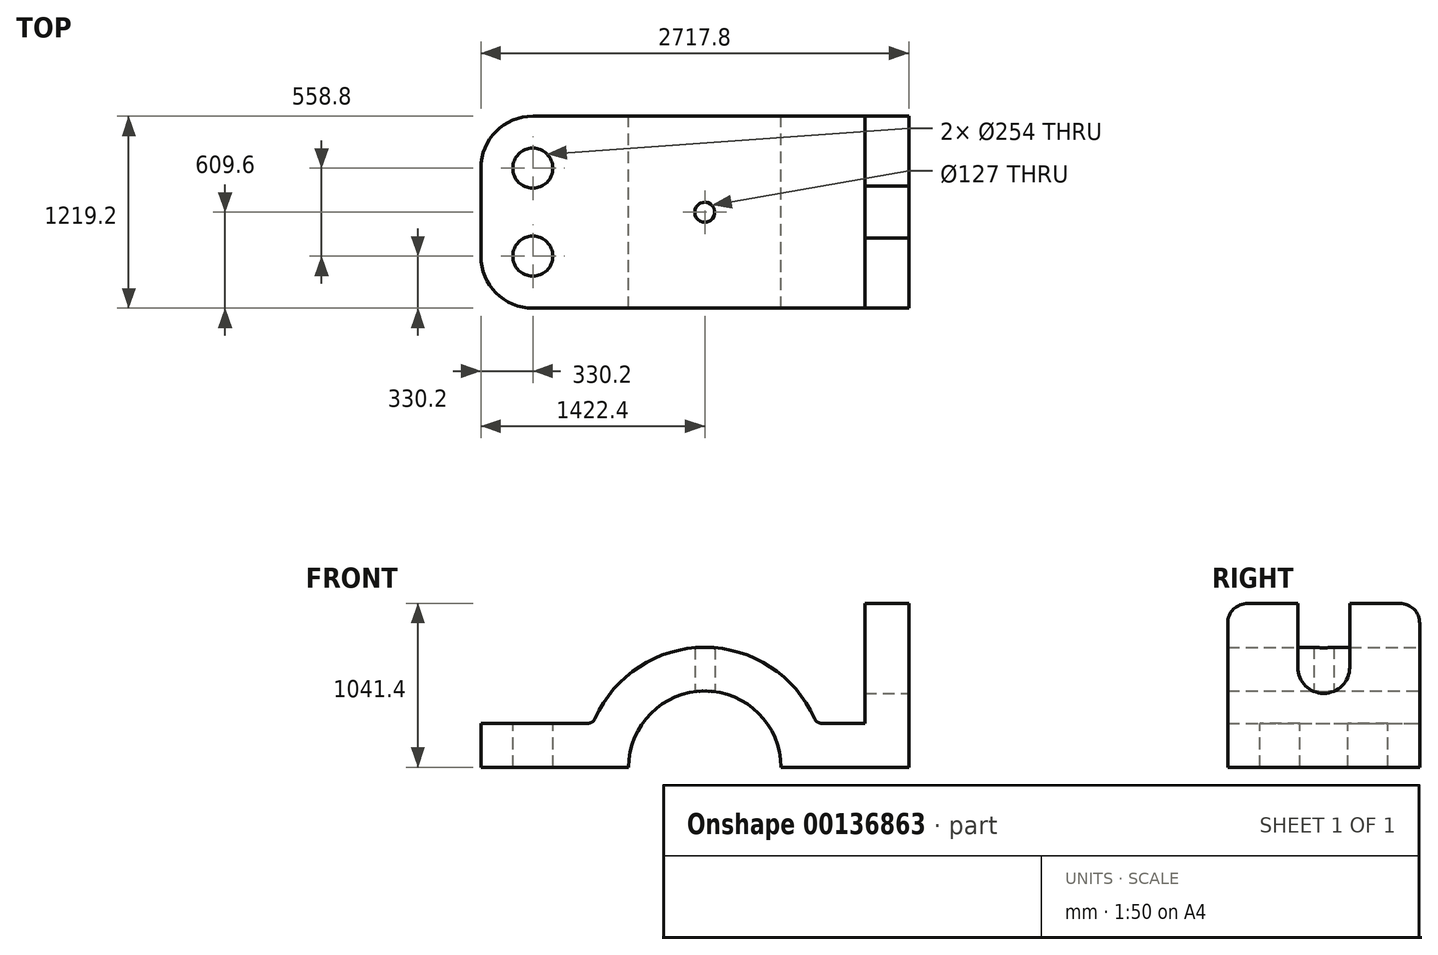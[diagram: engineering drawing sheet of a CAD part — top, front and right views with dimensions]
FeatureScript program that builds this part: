
annotation { "Feature Type Name" : "Feature", "Feature Type Description" : "" }
export const myFeature = defineFeature(function(context is Context, id is Id, definition is map)
    precondition{}
    {
        {
            var Q0;
            Q0=qCreatedBy(makeId("Front.planeOp"),FACE);
            var sketch = newSketch(context, id + "F0", { "sketchPlane" : qUnion([Q0])});
            skLineSegment(sketch, "E0.bottom", {"start": v(1358.9, -139.7) * mm, "end": v(547.37, -139.7) * mm});
            skLineSegment(sketch, "E0.top", {"start": v(1079.5, 139.7) * mm, "end": v(772.43, 139.7) * mm});
            skLineSegment(sketch, "E0.left", {"start": v(1358.9, -139.7) * mm, "end": v(1358.9, 139.7) * mm});
            skLineSegment(sketch, "E0.right", {"start": v(-1358.9, -139.7) * mm, "end": v(-1358.9, 139.7) * mm});
            skPoint(sketch, "E0.middle", {"position": v(0, 0) * mm});
            skArc(sketch, "E1", {"start": v(772.43, 139.7) * mm, "mid": v(63.5, 622.3) * mm, "end": v(-645.43, 139.7) * mm});
            skArc(sketch, "E2", {"start": v(547.37, -139.7) * mm, "mid": v(63.5, 344.17) * mm, "end": v(-420.37, -139.7) * mm});
            skLineSegment(sketch, "E3.trimOffspring", {"start": v(-420.37, -139.7) * mm, "end": v(-1358.9, -139.7) * mm});
            skLineSegment(sketch, "E4.trimOffspring", {"start": v(-645.43, 139.7) * mm, "end": v(-1358.9, 139.7) * mm});
            skLineSegment(sketch, "E5.top", {"start": v(1358.9, 901.7) * mm, "end": v(1079.5, 901.7) * mm});
            skLineSegment(sketch, "E5.left", {"start": v(1358.9, 139.7) * mm, "end": v(1358.9, 901.7) * mm});
            skLineSegment(sketch, "E5.right", {"start": v(1079.5, 139.7) * mm, "end": v(1079.5, 901.7) * mm});
            skSolve(sketch);
        }
        {
            var Q0;
            Q0 = qSketchRegion(id + "F0", true);
            extrude(context, id + "F1", {"entities" : qUnion([Q0]), "depth" : 1219.2 * mm});
        }
        {
            var Q0;
            Q0=makeQuery(id+"F1.opExtrude","CAP_EDGE",EDGE,{"disambiguationData":[OSD([sQuery(id+"F0.wireOp",EDGE,"E0.right")])],"isStart":false});
            var Q1;
            Q1=makeQuery(id+"F1.opExtrude","CAP_EDGE",EDGE,{"disambiguationData":[OSD([sQuery(id+"F0.wireOp",EDGE,"E0.right")])],"isStart":true});
            fillet(context, id + "F2", {"entities" : qUnion([Q0, Q1]), "radius" : 330.2 * mm, "tangentPropagation" : true, "allowEdgeOverflow" : false});
        }
        {
            var Q0;
            Q0=makeQuery(id+"F1.opExtrude","SWEPT_FACE",FACE,{"disambiguationData":[OSD([sQuery(id+"F0.wireOp",EDGE,"E0.left"),sQuery(id+"F0.wireOp",EDGE,"E5.left")])]});
            var sketch = newSketch(context, id + "F3", { "sketchPlane" : qUnion([Q0])});
            skArc(sketch, "E6", {"start": v(-774.7, 495.3) * mm, "mid": v(-609.6, 330.2) * mm, "end": v(-444.5, 495.3) * mm});
            skLineSegment(sketch, "E7", {"start": v(-774.7, 495.3) * mm, "end": v(-774.7, 901.7) * mm});
            skLineSegment(sketch, "E8", {"start": v(-444.5, 495.3) * mm, "end": v(-444.5, 901.7) * mm});
            skSolve(sketch);
        }
        {
            var Q0;
            Q0=makeQuery(id+"F3.imprint","IMPRINT",FACE,{"disambiguationData":[TD([[makeQuery(id+"F3.imprint","IMPRINT",EDGE,{"derivedFrom":sQuery(id+"F3.wireOp",EDGE,"E6")}),1.0]])]});
            extrude(context, id + "F4", {"entities" : qUnion([Q0]), "operationType" : NewBodyOperationType.REMOVE, "endBound" : BoundingType.UP_TO_NEXT, "oppositeDirection" : true, "depth" : 25.4 * mm});
        }
        {
            var Q0;
            Q0=makeQuery(id+"F1.opExtrude","CAP_EDGE",EDGE,{"disambiguationData":[OSD([sQuery(id+"F0.wireOp",EDGE,"E5.top")])],"isStart":false});
            var Q1;
            Q1=makeQuery(id+"F1.opExtrude","CAP_EDGE",EDGE,{"disambiguationData":[OSD([sQuery(id+"F0.wireOp",EDGE,"E5.top")])],"isStart":true});
            fillet(context, id + "F5", {"entities" : qUnion([Q0, Q1]), "radius" : 127 * mm, "tangentPropagation" : true, "allowEdgeOverflow" : false});
        }
        {
            var Q0;
            Q0=makeQuery(id+"F1.opExtrude","SWEPT_EDGE",EDGE,{"disambiguationData":[OSD([sQuery(id+"F0.wireOp",EDGE,"E0.top"),sQuery(id+"F0.wireOp",EDGE,"E1")])]});
            var Q1;
            Q1=makeQuery(id+"F1.opExtrude","SWEPT_EDGE",EDGE,{"disambiguationData":[OSD([sQuery(id+"F0.wireOp",EDGE,"E1"),sQuery(id+"F0.wireOp",EDGE,"E4.trimOffspring")])]});
            fillet(context, id + "F6", {"entities" : qUnion([Q0, Q1]), "radius" : 50.8 * mm, "tangentPropagation" : true, "allowEdgeOverflow" : false});
        }
        {
            var Q0;
            Q0=makeQuery(id+"F1.opExtrude","SWEPT_FACE",FACE,{"disambiguationData":[OSD([sQuery(id+"F0.wireOp",EDGE,"E4.trimOffspring")])]});
            var sketch = newSketch(context, id + "F7", { "sketchPlane" : qUnion([Q0])});
            skCircle(sketch, "E9", {"center": v(-1028.7, -889) * mm, "radius": 127 * mm});
            skCircle(sketch, "E10", {"center": v(-1028.7, -330.2) * mm, "radius": 127 * mm});
            skSolve(sketch);
        }
        {
            var Q0;
            Q0 = qSketchRegion(id + "F7", true);
            extrude(context, id + "F8", {"entities" : qUnion([Q0]), "operationType" : NewBodyOperationType.REMOVE, "endBound" : BoundingType.THROUGH_ALL, "oppositeDirection" : true, "depth" : 25.4 * mm});
        }
        {
            var Q0;
            Q0=qCreatedBy(makeId("Top.planeOp"),FACE);
            var sketch = newSketch(context, id + "F9", { "sketchPlane" : qUnion([Q0])});
            skCircle(sketch, "E11", {"center": v(63.5, -609.6) * mm, "radius": 63.5 * mm});
            skSolve(sketch);
        }
        {
            var Q0;
            Q0 = qSketchRegion(id + "F9", true);
            extrude(context, id + "F10", {"entities" : qUnion([Q0]), "operationType" : NewBodyOperationType.REMOVE, "depth" : 889 * mm});
        }
    });
